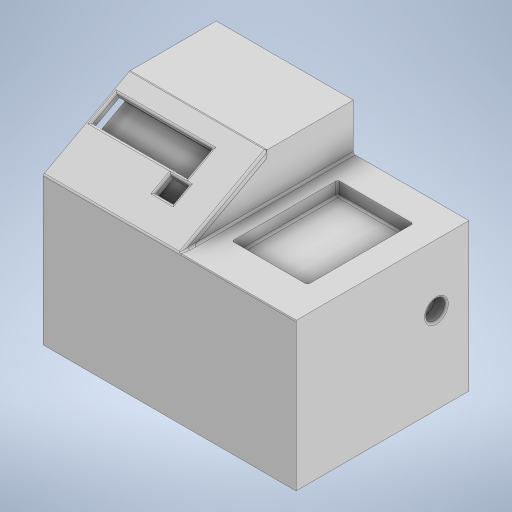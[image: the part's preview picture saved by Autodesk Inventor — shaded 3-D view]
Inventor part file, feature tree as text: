
AUTODESK INVENTOR PART (.ipt)
format: ipt  version: 2024 (Build 280153000, 153)  size: 507,904 bytes
history: native  units: mm
features: extrude x13, sketch x12, projected_geometry x11, fillet x1
ambient origin geometry x8: Origin, YZ Plane, XZ Plane, XY Plane, X Axis, Y Axis, Z Axis, Center Point
bodies: Solid1 (feature_tree)
feature tree (37):
  extrude  "Extrusion1"  Depth=65.0mm
  extrude  "Extrusion2"  Depth=130.0mm
  extrude  "Extrusion3"  Depth=48.0mm
  extrude  "Extrusion4"  Depth=96.0mm
  extrude  "Extrusion5"  Depth=11.0mm
  extrude  "Extrusion6"  Depth=131.0mm
  extrude  "Extrusion7"  Depth=10.0mm
  extrude  "Extrusion8"  Depth=10.0mm
  extrude  "Extrusion9"  Depth=85.0mm TaperAngle=0.0deg
  sketch  "Sketch10"  dims[d23=47.5mm d24=35.5mm]
  extrude  "Extrusion10"  Depth=35.5mm
  extrude  "Extrusion12"  Depth=71.0mm
  extrude  "Extrusion13"  Depth=10.0mm TaperAngle=0.0deg
  fillet  "Fillet1"  Radius=15.0mm
  extrude  "Extrusion14"  Depth=12.0mm TaperAngle=0.0deg
  sketch  "Sketch1"  dims[d0=95.0mm d1=65.0mm]
  sketch  "Sketch2"  dims[d5=190.0mm d6=130.0mm]
  sketch  "Sketch3"  dims[d7=65.5mm d8=48.0mm]
  projected_geometry  "Projected Loop1"
  sketch  "Sketch4"  dims[d9=131.0mm d10=96.0mm]
  projected_geometry  "Projected Loop2"
  sketch  "Sketch5"  dims[d11=11.0mm d12=0.0mm d13=65.5mm]
  projected_geometry  "Projected Loop3"
  sketch  "Sketch6"  dims[d14=48.0mm d15=131.0mm]
  projected_geometry  "Projected Loop4"
  projected_geometry  "Projected Loop5"
  projected_geometry  "Projected Loop6"
  sketch  "Sketch7"  dims[d16=96.0mm d17=10.0mm]
  sketch  "Sketch8"  dims[d18=10.0mm d19=10.0mm]
  projected_geometry  "Projected Loop7"
  projected_geometry  "Projected Loop8"
  projected_geometry  "Projected Loop9"
  sketch  "Sketch9"  dims[d20=10.0mm d21=85.0mm d22=0.0mm]
  projected_geometry  "Projected Loop10"
  sketch  "Sketch11"  dims[d25=21.5mm d26=71.0mm]
  projected_geometry  "Projected Loop11"
  sketch  "Sketch12"  dims[d27=15.0mm d28=0.0mm d29=10.0mm d30=0.0mm d31=15.0mm d32=202.5mm d33=0.0mm d34=10.0mm d35=50.0mm d36=0.0mm d37=15.0mm d38=0.0mm d39=103.0mm d40=0.0mm d41=8.0mm d42=0.0mm d43=48.0mm d44=1.6mm d45=10.052mm d46=8.3mm d47=40.0mm d48=190.0mm d49=0.0mm d52=95.0mm d53=0.0mm d56=14.0mm d58=13.4mm d59=72.0mm d60=21.5mm d61=72.0mm d62=10.0mm d63=0.0mm d64=1.5mm d65=146.0mm d66=130.0mm d67=65.0mm d68=70.0mm d69=2.0mm d70=15.0mm d71=6.0mm d72=30.0mm d73=70.0mm d74=2.0mm d75=15.0mm d76=6.0mm d77=30.0mm d78=2.0mm d79=20.0mm d80=6.0mm d81=40.0mm d82=12.0mm d83=0.0mm]
